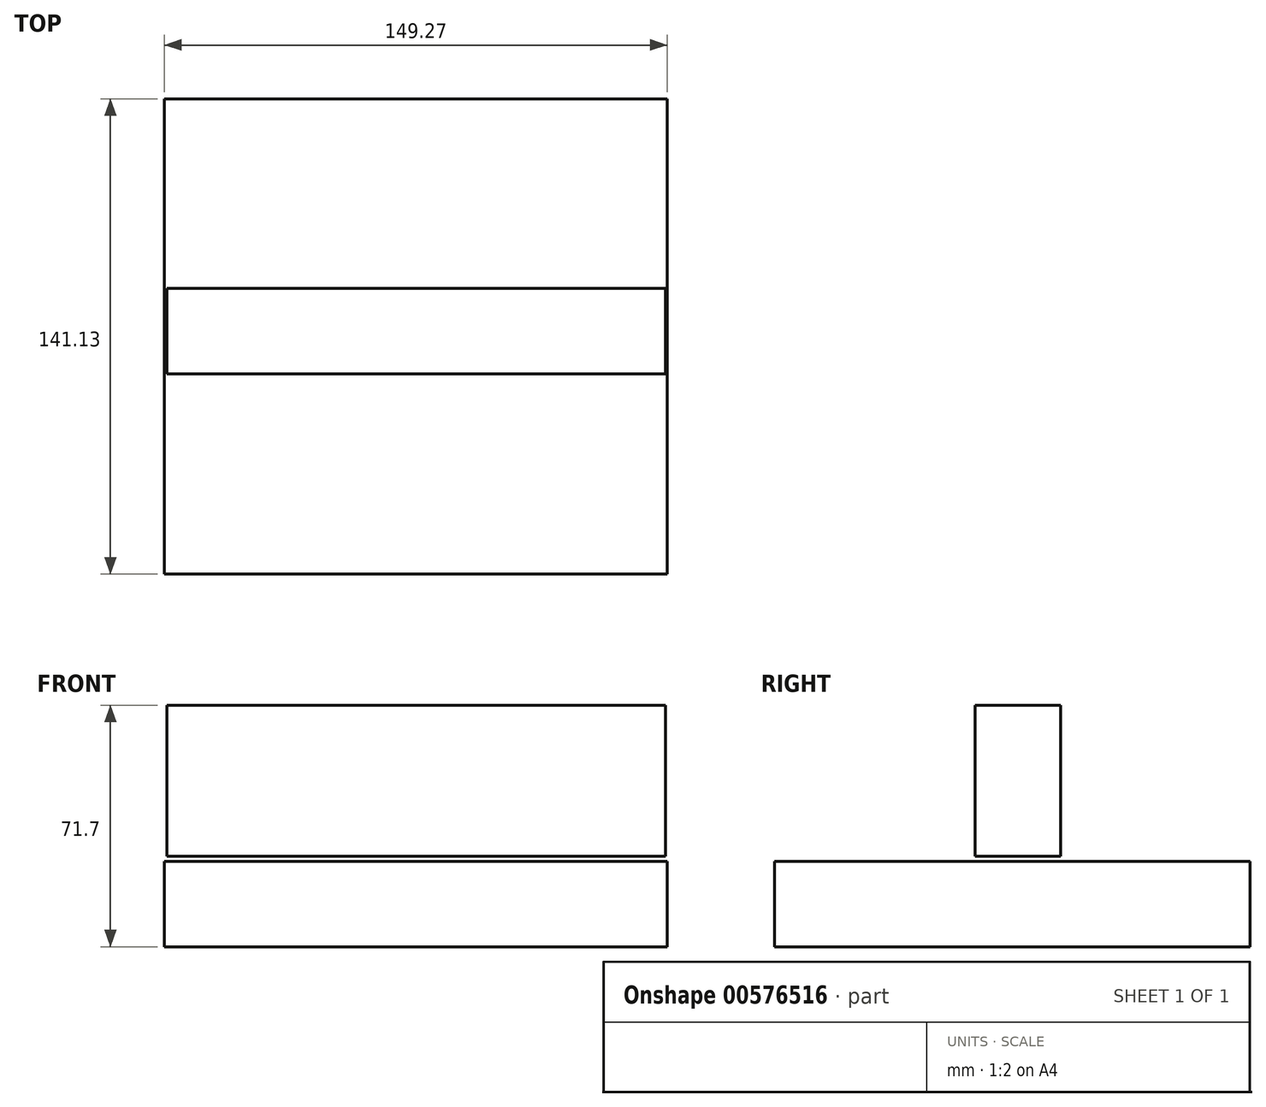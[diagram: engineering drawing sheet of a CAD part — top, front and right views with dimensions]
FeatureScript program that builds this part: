
annotation { "Feature Type Name" : "Feature", "Feature Type Description" : "" }
export const myFeature = defineFeature(function(context is Context, id is Id, definition is map)
    precondition{}
    {
        {
            var Q0;
            Q0=qCreatedBy(makeId("Top.planeOp"),FACE);
            var sketch = newSketch(context, id + "F0", { "sketchPlane" : qUnion([Q0])});
            skLineSegment(sketch, "E0.bottom", {"start": v(-74.74, 68.94) * mm, "end": v(74.53, 68.94) * mm});
            skLineSegment(sketch, "E0.top", {"start": v(-74.74, -72.2) * mm, "end": v(74.53, -72.2) * mm});
            skLineSegment(sketch, "E0.left", {"start": v(-74.74, 68.94) * mm, "end": v(-74.74, -72.2) * mm});
            skLineSegment(sketch, "E0.right", {"start": v(74.53, 68.94) * mm, "end": v(74.53, -72.2) * mm});
            skSolve(sketch);
        }
        {
            var Q0;
            Q0=makeQuery(id+"F0.imprint","IMPRINT",FACE,{"disambiguationData":[TD([[makeQuery(id+"F0.imprint","IMPRINT",EDGE,{"derivedFrom":sQuery(id+"F0.wireOp",EDGE,"E0.bottom")}),-1.0]])]});
            extrude(context, id + "F1", {"entities" : qUnion([Q0]), "depth" : 25.4 * mm, "offsetDistance" : 25.4 * mm});
        }
        {
            var Q0;
            Q0=qCreatedBy(makeId("Front.planeOp"),FACE);
            var sketch = newSketch(context, id + "F2", { "sketchPlane" : qUnion([Q0])});
            skLineSegment(sketch, "E1.bottom", {"start": v(-74.04, 71.7) * mm, "end": v(74.04, 71.7) * mm});
            skLineSegment(sketch, "E1.top", {"start": v(-74.04, 26.82) * mm, "end": v(74.04, 26.82) * mm});
            skLineSegment(sketch, "E1.left", {"start": v(-74.04, 71.7) * mm, "end": v(-74.04, 26.82) * mm});
            skLineSegment(sketch, "E1.right", {"start": v(74.04, 71.7) * mm, "end": v(74.04, 26.82) * mm});
            skSolve(sketch);
        }
        {
            var Q0;
            Q0=makeQuery(id+"F2.imprint","IMPRINT",FACE,{"disambiguationData":[TD([[makeQuery(id+"F2.imprint","IMPRINT",EDGE,{"derivedFrom":sQuery(id+"F2.wireOp",EDGE,"E1.bottom")}),-1.0]])]});
            extrude(context, id + "F3", {"entities" : qUnion([Q0]), "endBound" : BoundingType.SYMMETRIC, "depth" : 25.4 * mm, "offsetDistance" : 25.4 * mm});
        }
    });
